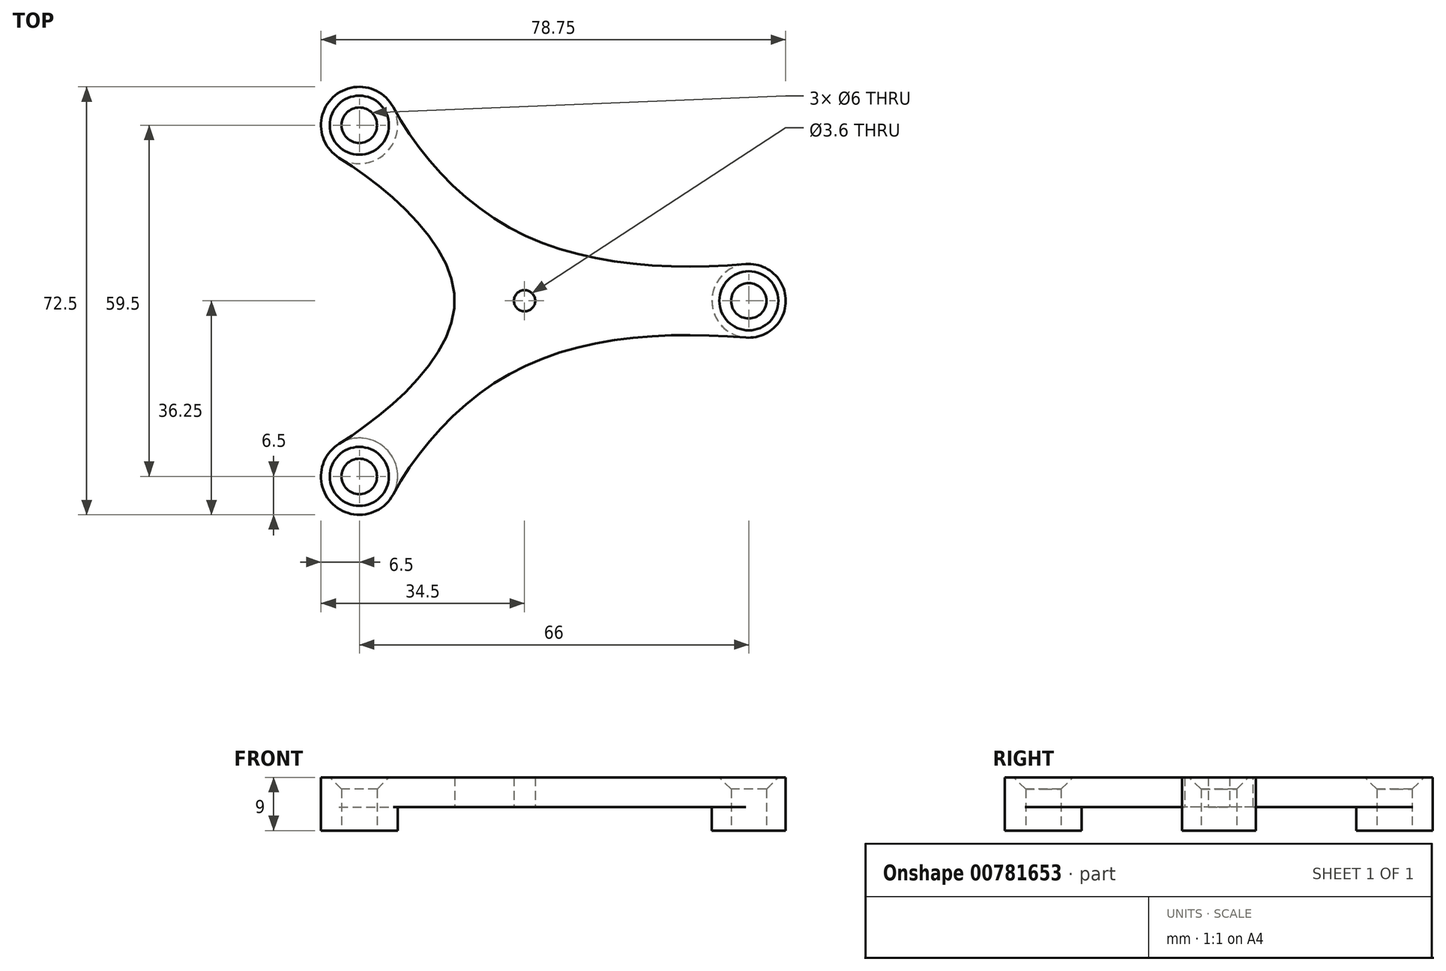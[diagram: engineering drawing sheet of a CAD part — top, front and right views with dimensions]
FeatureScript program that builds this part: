
annotation { "Feature Type Name" : "Feature", "Feature Type Description" : "" }
export const myFeature = defineFeature(function(context is Context, id is Id, definition is map)
    precondition{}
    {
        {
            var Q0;
            Q0=qCreatedBy(makeId("Top.planeOp"),FACE);
            var sketch = newSketch(context, id + "F0", { "sketchPlane" : qUnion([Q0])});
            skLineSegment(sketch, "E0", {"start": v(-155.74, 0) * mm, "end": v(93.44, 0) * mm, "construction": true});
            skCircle(sketch, "E1", {"center": v(-28, 29.75) * mm, "radius": 5.25 * mm, "construction": true});
            skCircle(sketch, "E2.MirrorC", {"center": v(-28, -29.75) * mm, "radius": 5.25 * mm, "construction": true});
            skCircle(sketch, "E3", {"center": v(-28, 29.75) * mm, "radius": 6.5 * mm});
            skCircle(sketch, "E4.MirrorC", {"center": v(-28, -29.75) * mm, "radius": 6.5 * mm});
            skPoint(sketch, "E5.centerSnap0", {"position": v(-34.42, 35.41) * mm});
            skFitSpline(sketch, "E6", {"points": [v(-22.28, 32.84) * mm, v(0, 11.08) * mm, v(37.47, 6.23) * mm], "startDerivative": vector(28.5, -52.7) * mm, "endDerivative": vector(70.13, 5.92) * mm});
            skFitSpline(sketch, "E7.MirrorCS", {"points": [v(-22.28, -32.84) * mm, v(0, -11.08) * mm, v(37.47, -6.23) * mm], "startDerivative": vector(28.5, 52.7) * mm, "endDerivative": vector(70.13, -5.92) * mm});
            skFitSpline(sketch, "E8", {"points": [v(-31.43, 24.23) * mm, v(-11.85, 0) * mm, v(-31.43, -24.23) * mm], "startDerivative": vector(48.43, -30.12) * mm, "endDerivative": vector(-48.43, -30.12) * mm});
            skCircle(sketch, "E9", {"center": v(0, 0) * mm, "radius": 1.8 * mm});
            skCircle(sketch, "E10", {"center": v(38, 0) * mm, "radius": 6.25 * mm});
            skCircle(sketch, "E11", {"center": v(38, 0) * mm, "radius": 3 * mm});
            skCircle(sketch, "E12", {"center": v(-28, 29.75) * mm, "radius": 3 * mm});
            skCircle(sketch, "E13", {"center": v(-28, -29.75) * mm, "radius": 3 * mm});
            skLineSegment(sketch, "E14", {"start": v(-28, 56.8) * mm, "end": v(-28, -41.38) * mm, "construction": true});
            skLineSegment(sketch, "E15", {"start": v(38, 62.26) * mm, "end": v(38, -42.02) * mm, "construction": true});
            skLineSegment(sketch, "E16", {"start": v(-28, 29.75) * mm, "end": v(0, 0) * mm, "construction": true});
            skLineSegment(sketch, "E17", {"start": v(0, 0) * mm, "end": v(-28, -29.75) * mm, "construction": true});
            skLineSegment(sketch, "E18", {"start": v(-11.21, 30.65) * mm, "end": v(-32.08, 11) * mm, "construction": true});
            skLineSegment(sketch, "E19", {"start": v(-28.1, -14.75) * mm, "end": v(-7.87, -33.79) * mm, "construction": true});
            skSolve(sketch);
        }
        {
            var Q0;
            {var subQ1=sQuery(id+"F0.wireOp",EDGE,"E6");Q0=makeQuery(id+"F0.imprint","IMPRINT",FACE,{"disambiguationData":[TD([[makeQuery(id+"F0.imprint","IMPRINT",EDGE,{"derivedFrom":subQ1}),-1.0]])]});}
            var Q1;
            Q1=makeQuery(id+"F0.imprint","IMPRINT",FACE,{"disambiguationData":[TD([[makeQuery(id+"F0.imprint","IMPRINT",EDGE,{"derivedFrom":sQuery(id+"F0.wireOp",EDGE,"E13")}),-1.0]])]});
            var Q2;
            Q2=makeQuery(id+"F0.imprint","IMPRINT",FACE,{"disambiguationData":[TD([[makeQuery(id+"F0.imprint","IMPRINT",EDGE,{"derivedFrom":sQuery(id+"F0.wireOp",EDGE,"E12")}),-1.0]])]});
            var Q3;
            {var subQ0=sQuery(id+"F0.wireOp",EDGE,"E10");Q3=makeQuery(id+"F0.imprint","IMPRINT",FACE,{"disambiguationData":[TD([[makeQuery(id+"F0.imprint","IMPRINT",EDGE,{"derivedFrom":subQ0}),1.0]])]});}
            extrude(context, id + "F1", {"entities" : qUnion([Q0, Q1, Q2, Q3]), "depth" : 5 * mm, "offsetDistance" : 25 * mm});
        }
        {
            var Q0;
            Q0=makeQuery(id+"F0.imprint","IMPRINT",FACE,{"disambiguationData":[TD([[makeQuery(id+"F0.imprint","IMPRINT",EDGE,{"derivedFrom":sQuery(id+"F0.wireOp",EDGE,"E13")}),-1.0]])]});
            var Q1;
            Q1=makeQuery(id+"F0.imprint","IMPRINT",FACE,{"disambiguationData":[TD([[makeQuery(id+"F0.imprint","IMPRINT",EDGE,{"derivedFrom":sQuery(id+"F0.wireOp",EDGE,"E12")}),-1.0]])]});
            var Q2;
            {var subQ0=sQuery(id+"F0.wireOp",EDGE,"E10");Q2=makeQuery(id+"F0.imprint","IMPRINT",FACE,{"disambiguationData":[TD([[makeQuery(id+"F0.imprint","IMPRINT",EDGE,{"derivedFrom":subQ0}),1.0]])]});}
            extrude(context, id + "F2", {"entities" : qUnion([Q0, Q1, Q2]), "operationType" : NewBodyOperationType.ADD, "oppositeDirection" : true, "depth" : 4 * mm, "offsetDistance" : 25 * mm});
        }
        {
            var Q0;
            Q0=makeQuery(id+"F1.opExtrude","CAP_EDGE",EDGE,{"disambiguationData":[OSD([sQuery(id+"F0.wireOp",EDGE,"E13")])],"isStart":false});
            var Q1;
            Q1=makeQuery(id+"F1.opExtrude","CAP_EDGE",EDGE,{"disambiguationData":[OSD([sQuery(id+"F0.wireOp",EDGE,"E12")])],"isStart":false});
            var Q2;
            Q2=makeQuery(id+"F1.opExtrude","CAP_EDGE",EDGE,{"disambiguationData":[OSD([sQuery(id+"F0.wireOp",EDGE,"E11")])],"isStart":false});
            chamfer(context, id + "F3", {"entities" : qUnion([Q0, Q1, Q2]), "width" : 2 * mm, "tangentPropagation" : true});
        }
    });
